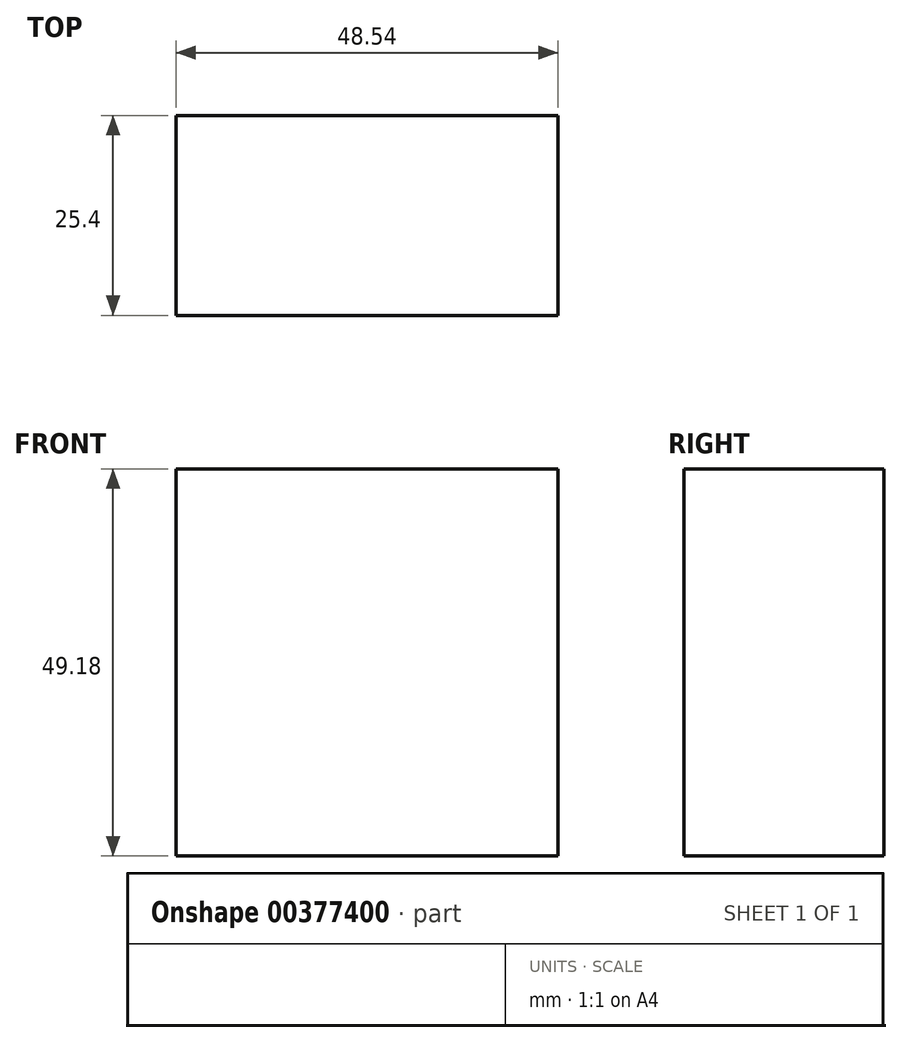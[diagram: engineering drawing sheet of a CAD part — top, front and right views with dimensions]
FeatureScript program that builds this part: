
annotation { "Feature Type Name" : "Feature", "Feature Type Description" : "" }
export const myFeature = defineFeature(function(context is Context, id is Id, definition is map)
    precondition{}
    {
        {
            var Q0;
            Q0=qCreatedBy(makeId("Front.planeOp"),FACE);
            var sketch = newSketch(context, id + "F0", { "sketchPlane" : qUnion([Q0])});
            skLineSegment(sketch, "E0.bottom", {"start": v(0, 0) * mm, "end": v(48.54, 0) * mm});
            skLineSegment(sketch, "E0.top", {"start": v(0, 49.18) * mm, "end": v(48.54, 49.18) * mm});
            skLineSegment(sketch, "E0.left", {"start": v(0, 0) * mm, "end": v(0, 49.18) * mm});
            skLineSegment(sketch, "E0.right", {"start": v(48.54, 0) * mm, "end": v(48.54, 49.18) * mm});
            skSolve(sketch);
        }
        {
            var Q0;
            Q0=makeQuery(id+"F0.imprint","IMPRINT",FACE,{"disambiguationData":[TD([[makeQuery(id+"F0.imprint","IMPRINT",EDGE,{"derivedFrom":sQuery(id+"F0.wireOp",EDGE,"E0.bottom")}),1.0]])]});
            var Q1;
            Q1 = qSketchRegion(id + "F0", true);
            extrude(context, id + "F1", {"entities" : qUnion([Q0, Q1]), "depth" : 25.4 * mm});
        }
    });
